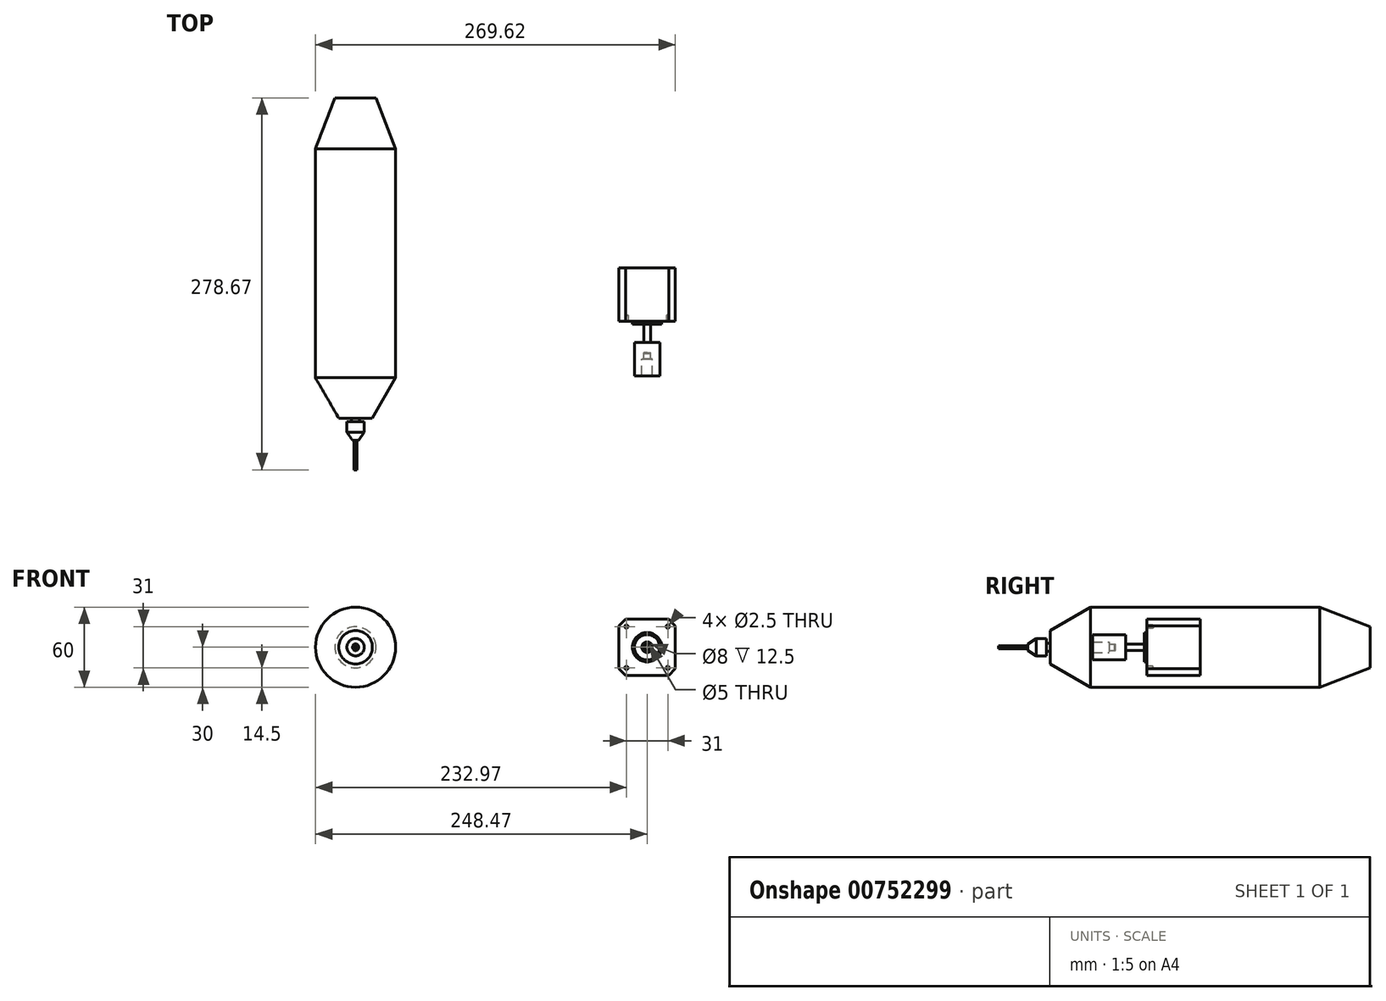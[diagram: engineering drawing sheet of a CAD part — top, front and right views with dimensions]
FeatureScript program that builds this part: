
annotation { "Feature Type Name" : "Feature", "Feature Type Description" : "" }
export const myFeature = defineFeature(function(context is Context, id is Id, definition is map)
    precondition{}
    {
        {
            var Q0;
            Q0=qCreatedBy(makeId("Front.planeOp"),FACE);
            var sketch = newSketch(context, id + "F0", { "sketchPlane" : qUnion([Q0])});
            skLineSegment(sketch, "E0.bottom", {"start": v(21.15, 21.15) * mm, "end": v(-21.15, 21.15) * mm});
            skLineSegment(sketch, "E0.top", {"start": v(21.15, -21.15) * mm, "end": v(-21.15, -21.15) * mm});
            skLineSegment(sketch, "E0.left", {"start": v(21.15, 21.15) * mm, "end": v(21.15, -21.15) * mm});
            skLineSegment(sketch, "E0.right", {"start": v(-21.15, 21.15) * mm, "end": v(-21.15, -21.15) * mm});
            skPoint(sketch, "E0.middle", {"position": v(0, 0) * mm});
            skCircle(sketch, "E1", {"center": v(0, 0) * mm, "radius": 11 * mm});
            skCircle(sketch, "E2", {"center": v(0, 0) * mm, "radius": 2.5 * mm});
            skLineSegment(sketch, "E3.bottom", {"start": v(-15.5, 15.5) * mm, "end": v(15.5, 15.5) * mm, "construction": true});
            skLineSegment(sketch, "E3.top", {"start": v(-15.5, -15.5) * mm, "end": v(15.5, -15.5) * mm, "construction": true});
            skLineSegment(sketch, "E3.left", {"start": v(-15.5, 15.5) * mm, "end": v(-15.5, -15.5) * mm, "construction": true});
            skLineSegment(sketch, "E3.right", {"start": v(15.5, 15.5) * mm, "end": v(15.5, -15.5) * mm, "construction": true});
            skPoint(sketch, "E4", {"position": v(-15.5, 15.5) * mm});
            skPoint(sketch, "E5", {"position": v(15.5, 15.5) * mm});
            skPoint(sketch, "E6", {"position": v(15.5, -15.5) * mm});
            skPoint(sketch, "E7", {"position": v(-15.5, -15.5) * mm});
            skSolve(sketch);
        }
        {
            var Q0;
            Q0 = qSketchRegion(id + "F0", true);
            var Q1;
            Q1=makeQuery(id+"F0.imprint","IMPRINT",FACE,{"disambiguationData":[TD([[makeQuery(id+"F0.imprint","IMPRINT",EDGE,{"derivedFrom":sQuery(id+"F0.wireOp",EDGE,"E1")}),1.0]])]});
            var Q2;
            Q2=makeQuery(id+"F0.imprint","IMPRINT",FACE,{"disambiguationData":[TD([[makeQuery(id+"F0.imprint","IMPRINT",EDGE,{"derivedFrom":sQuery(id+"F0.wireOp",EDGE,"E2")}),1.0]])]});
            extrude(context, id + "F1", {"entities" : qUnion([Q0, Q1, Q2]), "oppositeDirection" : true, "depth" : 40 * mm, "offsetDistance" : 25 * mm});
        }
        {
            var Q0;
            Q0=makeQuery(id+"F0.imprint","IMPRINT",FACE,{"disambiguationData":[TD([[makeQuery(id+"F0.imprint","IMPRINT",EDGE,{"derivedFrom":sQuery(id+"F0.wireOp",EDGE,"E1")}),1.0]])]});
            extrude(context, id + "F2", {"entities" : qUnion([Q0]), "operationType" : NewBodyOperationType.ADD, "depth" : 2 * mm, "offsetDistance" : 25 * mm});
        }
        {
            var Q0;
            Q0=makeQuery(id+"F0.imprint","IMPRINT",FACE,{"disambiguationData":[TD([[makeQuery(id+"F0.imprint","IMPRINT",EDGE,{"derivedFrom":sQuery(id+"F0.wireOp",EDGE,"E2")}),1.0]])]});
            extrude(context, id + "F3", {"entities" : qUnion([Q0]), "operationType" : NewBodyOperationType.ADD, "depth" : 24 * mm, "offsetDistance" : 25 * mm});
        }
        {
            var Q0;
            Q0=makeQuery(id+"F1.opExtrude","SWEPT_EDGE",EDGE,{"disambiguationData":[OSD([sQuery(id+"F0.wireOp",EDGE,"E0.bottom"),sQuery(id+"F0.wireOp",EDGE,"E0.left")])]});
            var Q1;
            Q1=makeQuery(id+"F1.opExtrude","SWEPT_EDGE",EDGE,{"disambiguationData":[OSD([sQuery(id+"F0.wireOp",EDGE,"E0.bottom"),sQuery(id+"F0.wireOp",EDGE,"E0.right")])]});
            var Q2;
            Q2=makeQuery(id+"F1.opExtrude","SWEPT_EDGE",EDGE,{"disambiguationData":[OSD([sQuery(id+"F0.wireOp",EDGE,"E0.top"),sQuery(id+"F0.wireOp",EDGE,"E0.left")])]});
            var Q3;
            Q3=makeQuery(id+"F1.opExtrude","SWEPT_EDGE",EDGE,{"disambiguationData":[OSD([sQuery(id+"F0.wireOp",EDGE,"E0.top"),sQuery(id+"F0.wireOp",EDGE,"E0.right")])]});
            chamfer(context, id + "F4", {"entities" : qUnion([Q0, Q1, Q2, Q3]), "width" : 5 * mm, "tangentPropagation" : true});
        }
        {
            var Q0;
            Q0=sQuery(id+"F0.wireOp",VERTEX,"E4");
            var Q1;
            Q1=sQuery(id+"F0.wireOp",VERTEX,"E5");
            var Q2;
            Q2=sQuery(id+"F0.wireOp",VERTEX,"E6");
            var Q3;
            Q3=sQuery(id+"F0.wireOp",VERTEX,"E7");
            var Q4;
            Q4=makeQuery(id+"F1.opExtrude","SWEPT_BODY",BODY,{"disambiguationData":[OSD([sQuery(id+"F0.wireOp",EDGE,"E0.bottom"),sQuery(id+"F0.wireOp",EDGE,"E0.top"),sQuery(id+"F0.wireOp",EDGE,"E0.left"),sQuery(id+"F0.wireOp",EDGE,"E0.right")])]});
            hole(context, id + "F5", {"style" : HoleStyle.SIMPLE, "endStyle" : HoleEndStyle.BLIND, "standardTappedOrClearance" : lookupTablePath({ "standard" : "ISO", "engagement" : "75%", "pitch" : "0.5 mm", "size" : "M3", "type" : "Tapped" }), "standardBlindInLast" : lookupTablePath({ "standard" : "ISO", "engagement" : "75%", "pitch" : "0.5 mm", "size" : "M3", "type" : "Tapped" }), "holeDiameter" : 2.5 * mm, "majorDiameter" : 3 * mm, "showTappedDepth" : true, "holeDepth" : 4.5 * mm, "isTappedThrough" : true, "tappedDepth" : 3 * mm, "tapClearance" : 3, "locations" : qUnion([Q0, Q1, Q2, Q3]), "scope" : qUnion([Q4])});
        }
        {
            var Q0;
            Q0=makeQuery(id+"F3.opExtrude","CAP_EDGE",EDGE,{"disambiguationData":[OSD([sQuery(id+"F0.wireOp",EDGE,"E2")])],"isStart":false});
            chamfer(context, id + "F6", {"entities" : qUnion([Q0]), "width" : .5 * mm, "tangentPropagation" : true});
        }
        {
            var Q0;
            Q0=qCreatedBy(makeId("Right.planeOp"),FACE);
            var sketch = newSketch(context, id + "F7", { "sketchPlane" : qUnion([Q0])});
            skLineSegment(sketch, "E8.bottom", {"start": v(-40.71, 0) * mm, "end": v(-15.71, 0) * mm});
            skLineSegment(sketch, "E8.top", {"start": v(-40.71, 9.5) * mm, "end": v(-15.71, 9.5) * mm});
            skLineSegment(sketch, "E8.left", {"start": v(-40.71, 0) * mm, "end": v(-40.71, 9.5) * mm});
            skLineSegment(sketch, "E8.right", {"start": v(-15.71, 0) * mm, "end": v(-15.71, 9.5) * mm});
            skLineSegment(sketch, "E9", {"start": v(30.39, 0) * mm, "end": v(-54.82, 0) * mm, "construction": true});
            skLineSegment(sketch, "E10", {"start": v(-15.71, 2.5) * mm, "end": v(-28.21, 2.5) * mm});
            skLineSegment(sketch, "E11", {"start": v(-28.21, 2.5) * mm, "end": v(-28.21, 4) * mm});
            skLineSegment(sketch, "E12", {"start": v(-28.21, 4) * mm, "end": v(-40.71, 4) * mm});
            skPoint(sketch, "E13", {"position": v(-28.21, 9.5) * mm});
            skSolve(sketch);
        }
        {
            var Q0;
            {var subQ1=sQuery(id+"F7.wireOp",EDGE,"E8.top");Q0=makeQuery(id+"F7.imprint","IMPRINT",FACE,{"disambiguationData":[TD([[makeQuery(id+"F7.imprint","IMPRINT",EDGE,{"derivedFrom":subQ1}),-1.0]])]});}
            var Q1;
            Q1=sQuery(id+"F7.wireOp",EDGE,"E9");
            revolve(context, id + "F8", {"operationType" : NewBodyOperationType.ADD, "surfaceOperationType" : NewSurfaceOperationType.NEW, "entities" : qUnion([Q0]), "axis" : qUnion([Q1]), "revolveType" : RevolveType.FULL});
        }
        {
            var Q0;
            Q0=qCreatedBy(makeId("Top.planeOp"),FACE);
            var sketch = newSketch(context, id + "F9", { "sketchPlane" : qUnion([Q0])});
            skLineSegment(sketch, "E14", {"start": v(-218.47, 109.07) * mm, "end": v(-218.47, -113.33) * mm, "construction": true});
            skLineSegment(sketch, "E15", {"start": v(-218.47, 167.47) * mm, "end": v(-203.07, 167.47) * mm});
            skLineSegment(sketch, "E16", {"start": v(-203.07, 167.47) * mm, "end": v(-188.47, 129.42) * mm});
            skLineSegment(sketch, "E17", {"start": v(-188.47, 129.42) * mm, "end": v(-188.47, -42.28) * mm});
            skLineSegment(sketch, "E18", {"start": v(-188.47, -42.28) * mm, "end": v(-205.87, -72.53) * mm});
            skLineSegment(sketch, "E19", {"start": v(-205.87, -72.53) * mm, "end": v(-215.5, -72.53) * mm});
            skLineSegment(sketch, "E20", {"start": v(-215.5, -72.53) * mm, "end": v(-215.5, -75.28) * mm});
            skLineSegment(sketch, "E21", {"start": v(-215.5, -75.28) * mm, "end": v(-211.96, -75.28) * mm});
            skLineSegment(sketch, "E22", {"start": v(-211.96, -75.28) * mm, "end": v(-211.96, -82.97) * mm});
            skLineSegment(sketch, "E23", {"start": v(-211.96, -82.97) * mm, "end": v(-216.2, -89.09) * mm});
            skLineSegment(sketch, "E24", {"start": v(-216.2, -89.09) * mm, "end": v(-218.47, -89.09) * mm});
            skLineSegment(sketch, "E25", {"start": v(-218.47, 167.47) * mm, "end": v(-218.47, -89.09) * mm});
            skLineSegment(sketch, "E26.bottom", {"start": v(-217.33, -89.09) * mm, "end": v(-218.47, -89.09) * mm});
            skLineSegment(sketch, "E26.top", {"start": v(-217.33, -111.2) * mm, "end": v(-218.47, -111.2) * mm});
            skLineSegment(sketch, "E26.left", {"start": v(-217.33, -89.09) * mm, "end": v(-217.33, -111.2) * mm});
            skLineSegment(sketch, "E26.right", {"start": v(-218.47, -89.09) * mm, "end": v(-218.47, -111.2) * mm});
            skSolve(sketch);
        }
        {
            var Q0;
            Q0 = qSketchRegion(id + "F9", true);
            var Q1;
            Q1=sQuery(id+"F9.wireOp",EDGE,"E14");
            revolve(context, id + "F10", {"surfaceOperationType" : NewSurfaceOperationType.NEW, "entities" : qUnion([Q0]), "axis" : qUnion([Q1]), "revolveType" : RevolveType.FULL});
        }
    });
